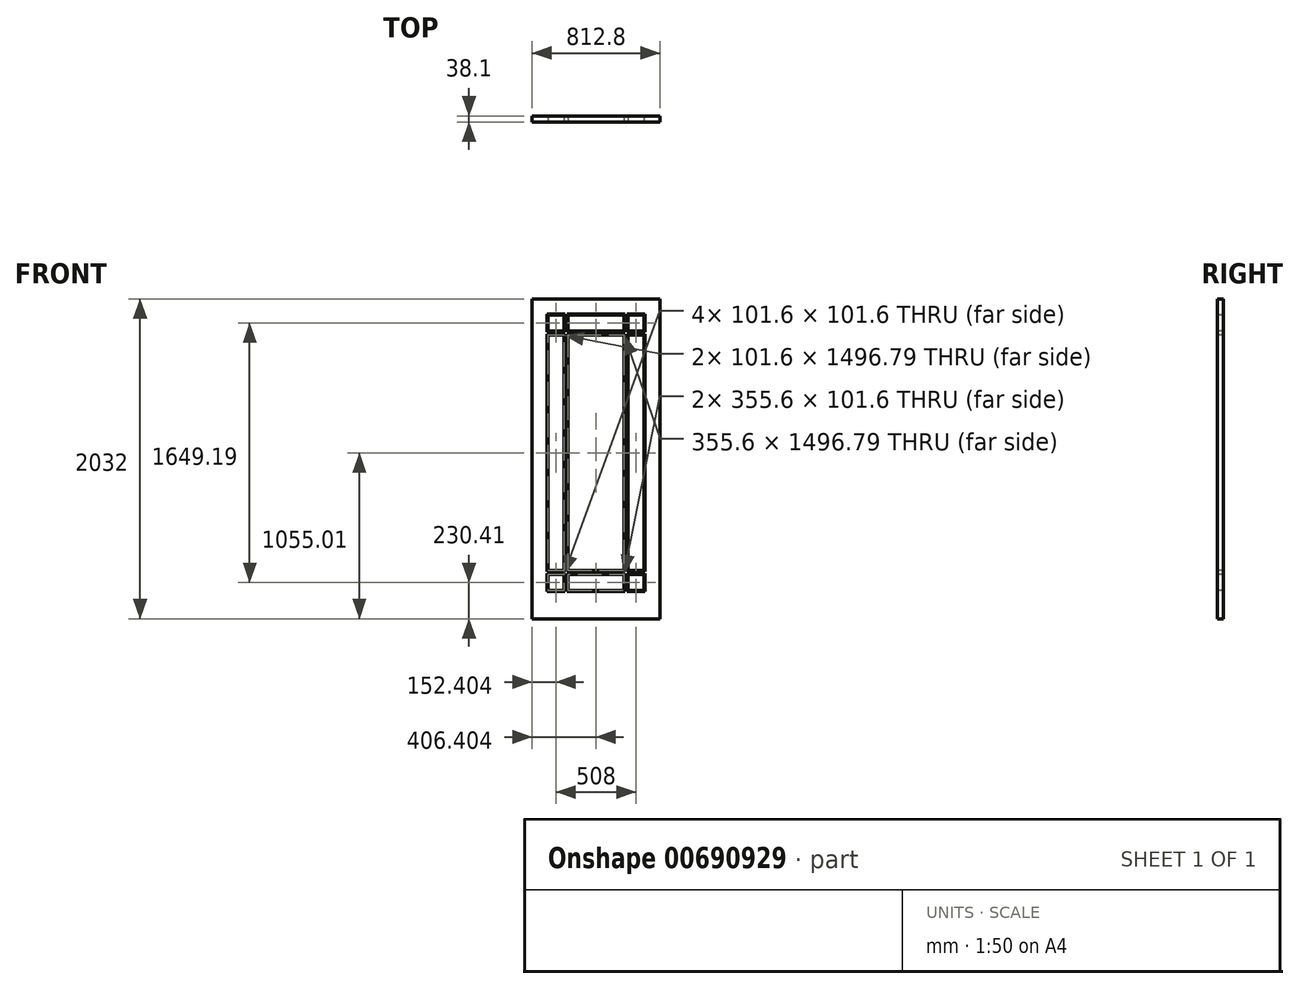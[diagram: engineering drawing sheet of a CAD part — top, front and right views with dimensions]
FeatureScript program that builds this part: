
annotation { "Feature Type Name" : "Feature", "Feature Type Description" : "" }
export const myFeature = defineFeature(function(context is Context, id is Id, definition is map)
    precondition{}
    {
        {
            var Q0;
            Q0=qCreatedBy(makeId("Front.planeOp"),FACE);
            var sketch = newSketch(context, id + "F0", { "sketchPlane" : qUnion([Q0])});
            skLineSegment(sketch, "E0.bottom", {"start": v(-419.25, 1193.72) * mm, "end": v(393.55, 1193.72) * mm});
            skLineSegment(sketch, "E0.top", {"start": v(-419.25, -838.28) * mm, "end": v(393.55, -838.28) * mm});
            skLineSegment(sketch, "E0.left", {"start": v(-419.25, 1193.72) * mm, "end": v(-419.25, -838.28) * mm});
            skLineSegment(sketch, "E0.right", {"start": v(393.55, 1193.72) * mm, "end": v(393.55, -838.28) * mm});
            skSolve(sketch);
        }
        {
            var Q0;
            Q0 = qSketchRegion(id + "F0", true);
            extrude(context, id + "F1", {"entities" : qUnion([Q0]), "depth" : 38.1 * mm, "offsetDistance" : 25.4 * mm});
        }
        {
            var Q0;
            Q0=makeQuery(id+"F1.opExtrude","CAP_FACE",FACE,{"disambiguationData":[OSD([sQuery(id+"F0.wireOp",EDGE,"E0.bottom"),sQuery(id+"F0.wireOp",EDGE,"E0.top"),sQuery(id+"F0.wireOp",EDGE,"E0.left"),sQuery(id+"F0.wireOp",EDGE,"E0.right")])],"isStart":false});
            var sketch = newSketch(context, id + "F2", { "sketchPlane" : qUnion([Q0])});
            skLineSegment(sketch, "E1.bottom", {"start": v(-317.65, 1092.12) * mm, "end": v(-216.05, 1092.12) * mm});
            skLineSegment(sketch, "E1.top", {"start": v(-317.65, 990.52) * mm, "end": v(-216.05, 990.52) * mm});
            skLineSegment(sketch, "E1.left", {"start": v(-317.65, 1092.12) * mm, "end": v(-317.65, 990.52) * mm});
            skLineSegment(sketch, "E1.right", {"start": v(-216.05, 1092.12) * mm, "end": v(-216.05, 990.52) * mm});
            skLineSegment(sketch, "E2.bottom", {"start": v(-190.65, 1092.12) * mm, "end": v(164.95, 1092.12) * mm});
            skLineSegment(sketch, "E2.top", {"start": v(-190.65, 990.52) * mm, "end": v(164.95, 990.52) * mm});
            skLineSegment(sketch, "E2.left", {"start": v(-190.65, 1092.12) * mm, "end": v(-190.65, 990.52) * mm});
            skLineSegment(sketch, "E2.right", {"start": v(164.95, 1092.12) * mm, "end": v(164.95, 990.52) * mm});
            skLineSegment(sketch, "E3.bottom", {"start": v(190.35, 1092.12) * mm, "end": v(291.95, 1092.12) * mm});
            skLineSegment(sketch, "E3.top", {"start": v(190.35, 990.52) * mm, "end": v(291.95, 990.52) * mm});
            skLineSegment(sketch, "E3.left", {"start": v(190.35, 1092.12) * mm, "end": v(190.35, 990.52) * mm});
            skLineSegment(sketch, "E3.right", {"start": v(291.95, 1092.12) * mm, "end": v(291.95, 990.52) * mm});
            skLineSegment(sketch, "E4.bottom", {"start": v(-317.65, 965.12) * mm, "end": v(-216.05, 965.12) * mm});
            skLineSegment(sketch, "E4.top", {"start": v(-317.65, -531.67) * mm, "end": v(-216.05, -531.67) * mm});
            skLineSegment(sketch, "E4.left", {"start": v(-317.65, 965.12) * mm, "end": v(-317.65, -531.67) * mm});
            skLineSegment(sketch, "E4.right", {"start": v(-216.05, 965.12) * mm, "end": v(-216.05, -531.67) * mm});
            skLineSegment(sketch, "E5.bottom", {"start": v(-190.65, 965.12) * mm, "end": v(164.95, 965.12) * mm});
            skLineSegment(sketch, "E5.top", {"start": v(-190.65, -531.67) * mm, "end": v(164.95, -531.67) * mm});
            skLineSegment(sketch, "E5.left", {"start": v(-190.65, 965.12) * mm, "end": v(-190.65, -531.67) * mm});
            skLineSegment(sketch, "E5.right", {"start": v(164.95, 965.12) * mm, "end": v(164.95, -531.67) * mm});
            skLineSegment(sketch, "E6.bottom", {"start": v(190.35, 965.12) * mm, "end": v(291.95, 965.12) * mm});
            skLineSegment(sketch, "E6.top", {"start": v(190.35, -531.67) * mm, "end": v(291.95, -531.67) * mm});
            skLineSegment(sketch, "E6.left", {"start": v(190.35, 965.12) * mm, "end": v(190.35, -531.67) * mm});
            skLineSegment(sketch, "E6.right", {"start": v(291.95, 965.12) * mm, "end": v(291.95, -531.67) * mm});
            skLineSegment(sketch, "E7.bottom", {"start": v(-190.65, -557.07) * mm, "end": v(164.95, -557.07) * mm});
            skLineSegment(sketch, "E7.top", {"start": v(-190.65, -658.67) * mm, "end": v(164.95, -658.67) * mm});
            skLineSegment(sketch, "E7.left", {"start": v(-190.65, -557.07) * mm, "end": v(-190.65, -658.67) * mm});
            skLineSegment(sketch, "E7.right", {"start": v(164.95, -557.07) * mm, "end": v(164.95, -658.67) * mm});
            skLineSegment(sketch, "E8.bottom", {"start": v(190.35, -557.07) * mm, "end": v(291.95, -557.07) * mm});
            skLineSegment(sketch, "E8.top", {"start": v(190.35, -658.67) * mm, "end": v(291.95, -658.67) * mm});
            skLineSegment(sketch, "E8.left", {"start": v(190.35, -557.07) * mm, "end": v(190.35, -658.67) * mm});
            skLineSegment(sketch, "E8.right", {"start": v(291.95, -557.07) * mm, "end": v(291.95, -658.67) * mm});
            skLineSegment(sketch, "E9.bottom", {"start": v(-216.05, -557.07) * mm, "end": v(-317.65, -557.07) * mm});
            skLineSegment(sketch, "E9.top", {"start": v(-216.05, -658.67) * mm, "end": v(-317.65, -658.67) * mm});
            skLineSegment(sketch, "E9.left", {"start": v(-216.05, -557.07) * mm, "end": v(-216.05, -658.67) * mm});
            skLineSegment(sketch, "E9.right", {"start": v(-317.65, -557.07) * mm, "end": v(-317.65, -658.67) * mm});
            skSolve(sketch);
        }
        {
            var Q0;
            Q0=makeQuery(id+"F2.imprint","IMPRINT",FACE,{"disambiguationData":[TD([[makeQuery(id+"F2.imprint","IMPRINT",EDGE,{"derivedFrom":sQuery(id+"F2.wireOp",EDGE,"E4.bottom")}),-1.0]])]});
            var sketch = newSketch(context, id + "F3", { "sketchPlane" : qUnion([Q0])});
            skLineSegment(sketch, "E10.0", {"start": v(-197, 971.47) * mm, "end": v(-197, -538.02) * mm});
            skLineSegment(sketch, "E10.1", {"start": v(171.3, 971.47) * mm, "end": v(-197, 971.47) * mm});
            skLineSegment(sketch, "E10.2", {"start": v(171.3, -538.02) * mm, "end": v(171.3, 971.47) * mm});
            skLineSegment(sketch, "E10.3", {"start": v(-197, -538.02) * mm, "end": v(171.3, -538.02) * mm});
            skLineSegment(sketch, "E11.0", {"start": v(-324, 971.47) * mm, "end": v(-324, -538.02) * mm});
            skLineSegment(sketch, "E11.1", {"start": v(-209.7, 971.47) * mm, "end": v(-324, 971.47) * mm});
            skLineSegment(sketch, "E11.2", {"start": v(-209.7, -538.02) * mm, "end": v(-209.7, 971.47) * mm});
            skLineSegment(sketch, "E11.3", {"start": v(-324, -538.02) * mm, "end": v(-209.7, -538.02) * mm});
            skLineSegment(sketch, "E12.0", {"start": v(-324, 1098.47) * mm, "end": v(-324, 984.17) * mm});
            skLineSegment(sketch, "E12.1", {"start": v(-209.7, 1098.47) * mm, "end": v(-324, 1098.47) * mm});
            skLineSegment(sketch, "E12.2", {"start": v(-209.7, 984.17) * mm, "end": v(-209.7, 1098.47) * mm});
            skLineSegment(sketch, "E12.3", {"start": v(-324, 984.17) * mm, "end": v(-209.7, 984.17) * mm});
            skLineSegment(sketch, "E13.0", {"start": v(-197, 1098.47) * mm, "end": v(-197, 984.17) * mm});
            skLineSegment(sketch, "E13.1", {"start": v(171.3, 1098.47) * mm, "end": v(-197, 1098.47) * mm});
            skLineSegment(sketch, "E13.2", {"start": v(171.3, 984.17) * mm, "end": v(171.3, 1098.47) * mm});
            skLineSegment(sketch, "E13.3", {"start": v(-197, 984.17) * mm, "end": v(171.3, 984.17) * mm});
            skLineSegment(sketch, "E14.0", {"start": v(184, 1098.47) * mm, "end": v(184, 984.17) * mm});
            skLineSegment(sketch, "E14.1", {"start": v(298.3, 1098.47) * mm, "end": v(184, 1098.47) * mm});
            skLineSegment(sketch, "E14.2", {"start": v(298.3, 984.17) * mm, "end": v(298.3, 1098.47) * mm});
            skLineSegment(sketch, "E14.3", {"start": v(184, 984.17) * mm, "end": v(298.3, 984.17) * mm});
            skLineSegment(sketch, "E15.0", {"start": v(184, 971.47) * mm, "end": v(184, -538.02) * mm});
            skLineSegment(sketch, "E15.1", {"start": v(298.3, 971.47) * mm, "end": v(184, 971.47) * mm});
            skLineSegment(sketch, "E15.2", {"start": v(298.3, -538.02) * mm, "end": v(298.3, 971.47) * mm});
            skLineSegment(sketch, "E15.3", {"start": v(184, -538.02) * mm, "end": v(298.3, -538.02) * mm});
            skLineSegment(sketch, "E16.0", {"start": v(184, -550.72) * mm, "end": v(184, -665.02) * mm});
            skLineSegment(sketch, "E16.1", {"start": v(298.3, -550.72) * mm, "end": v(184, -550.72) * mm});
            skLineSegment(sketch, "E16.2", {"start": v(298.3, -665.02) * mm, "end": v(298.3, -550.72) * mm});
            skLineSegment(sketch, "E16.3", {"start": v(184, -665.02) * mm, "end": v(298.3, -665.02) * mm});
            skLineSegment(sketch, "E17.0", {"start": v(-197, -550.72) * mm, "end": v(-197, -665.02) * mm});
            skLineSegment(sketch, "E17.1", {"start": v(171.3, -550.72) * mm, "end": v(-197, -550.72) * mm});
            skLineSegment(sketch, "E17.2", {"start": v(171.3, -665.02) * mm, "end": v(171.3, -550.72) * mm});
            skLineSegment(sketch, "E17.3", {"start": v(-197, -665.02) * mm, "end": v(171.3, -665.02) * mm});
            skLineSegment(sketch, "E18.0", {"start": v(-324, -665.02) * mm, "end": v(-209.7, -665.02) * mm});
            skLineSegment(sketch, "E18.1", {"start": v(-324, -550.72) * mm, "end": v(-324, -665.02) * mm});
            skLineSegment(sketch, "E18.2", {"start": v(-209.7, -550.72) * mm, "end": v(-324, -550.72) * mm});
            skLineSegment(sketch, "E18.3", {"start": v(-209.7, -665.02) * mm, "end": v(-209.7, -550.72) * mm});
            skSolve(sketch);
        }
        {
            var Q0;
            Q0 = qSketchRegion(id + "F2", true);
            extrude(context, id + "F4", {"entities" : qUnion([Q0]), "operationType" : NewBodyOperationType.REMOVE, "oppositeDirection" : true, "depth" : 309.88 * mm, "offsetDistance" : 25.4 * mm});
        }
        {
            var Q0;
            Q0 = qSketchRegion(id + "F3", true);
            extrude(context, id + "F5", {"entities" : qUnion([Q0]), "operationType" : NewBodyOperationType.REMOVE, "oppositeDirection" : true, "depth" : 2.54 * mm, "offsetDistance" : 25.4 * mm});
        }
    });
